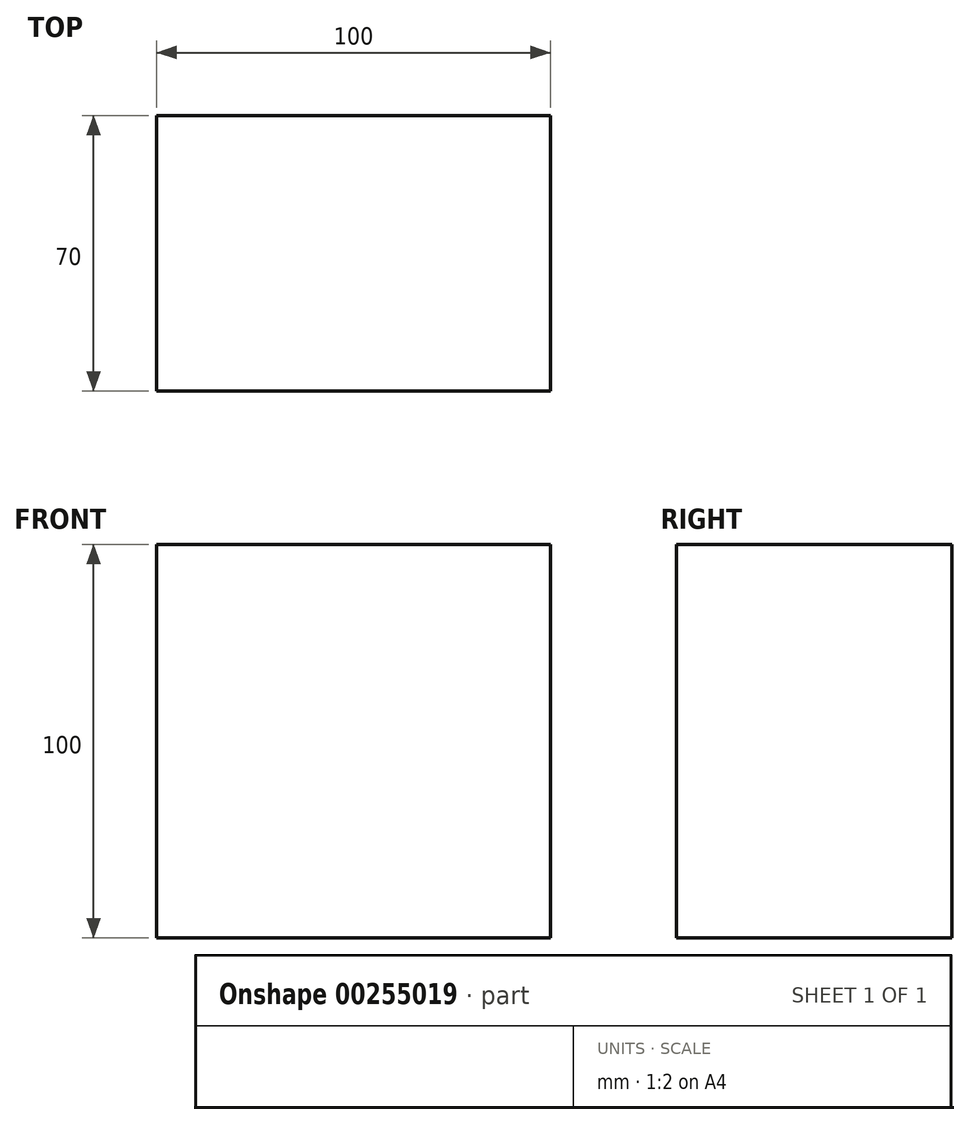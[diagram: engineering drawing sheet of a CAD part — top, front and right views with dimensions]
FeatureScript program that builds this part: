
annotation { "Feature Type Name" : "Feature", "Feature Type Description" : "" }
export const myFeature = defineFeature(function(context is Context, id is Id, definition is map)
    precondition{}
    {
        {
            var Q0;
            Q0=qCreatedBy(makeId("Front.planeOp"),FACE);
            var sketch = newSketch(context, id + "F0", { "sketchPlane" : qUnion([Q0])});
            skLineSegment(sketch, "E0.bottom", {"start": v(0, 0) * mm, "end": v(100, 0) * mm});
            skLineSegment(sketch, "E0.top", {"start": v(0, 100) * mm, "end": v(100, 100) * mm});
            skLineSegment(sketch, "E0.left", {"start": v(0, 0) * mm, "end": v(0, 100) * mm});
            skLineSegment(sketch, "E0.right", {"start": v(100, 0) * mm, "end": v(100, 100) * mm});
            skSolve(sketch);
        }
        {
            var Q0;
            Q0=makeQuery(id+"F0.imprint","IMPRINT",FACE,{"disambiguationData":[TD([[makeQuery(id+"F0.imprint","IMPRINT",EDGE,{"derivedFrom":sQuery(id+"F0.wireOp",EDGE,"E0.bottom")}),1.0]])]});
            extrude(context, id + "F1", {"entities" : qUnion([Q0]), "depth" : 70 * mm});
        }
    });
